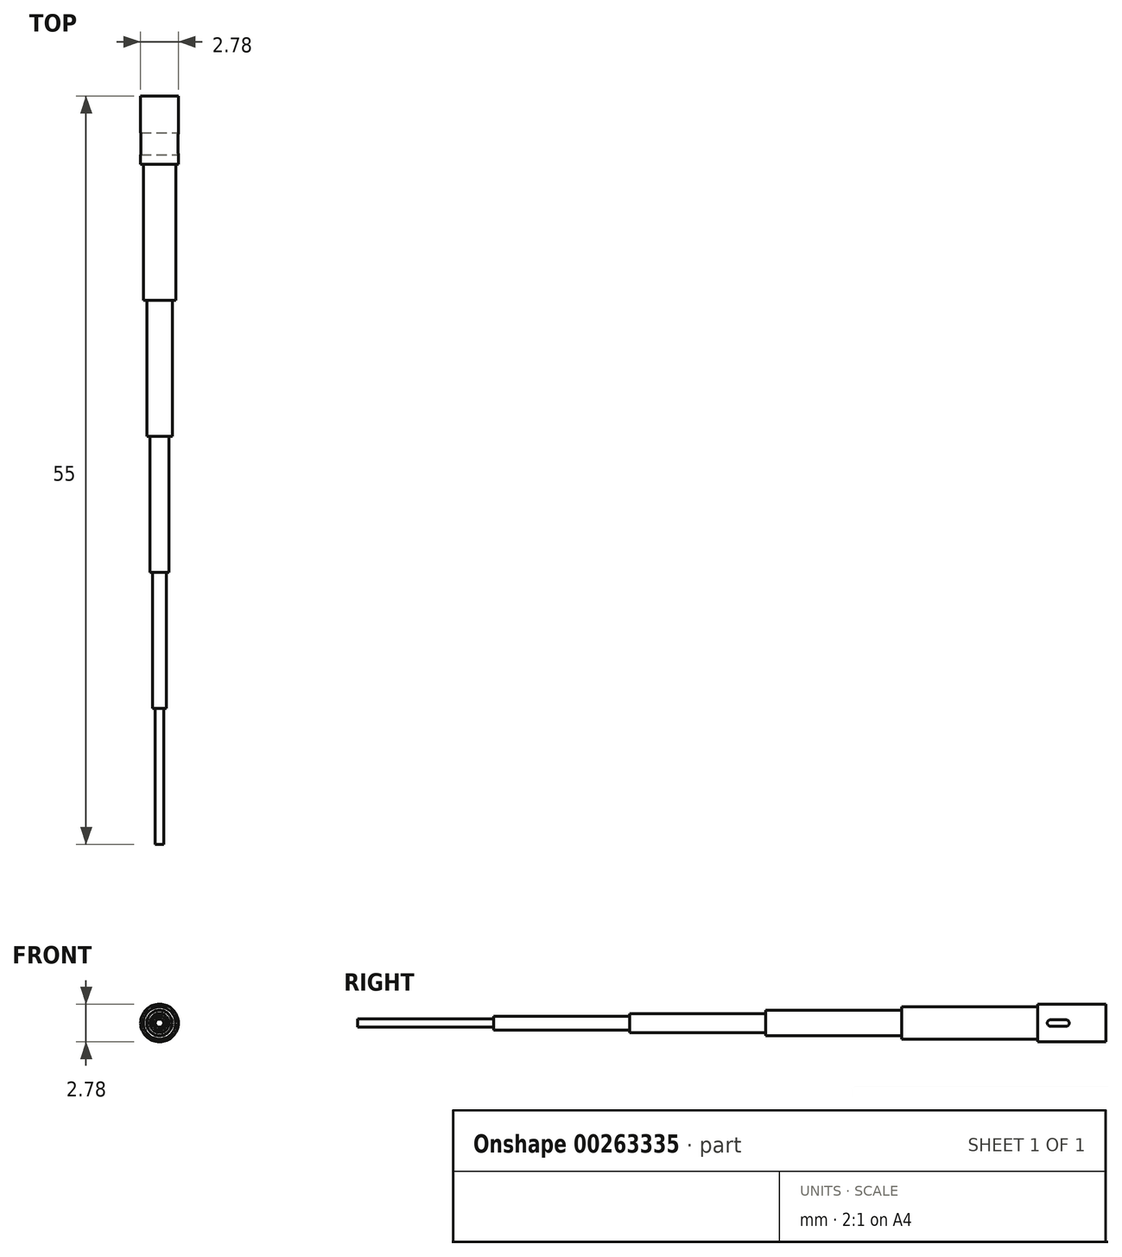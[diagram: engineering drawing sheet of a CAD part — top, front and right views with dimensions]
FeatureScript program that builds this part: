
annotation { "Feature Type Name" : "Feature", "Feature Type Description" : "" }
export const myFeature = defineFeature(function(context is Context, id is Id, definition is map)
    precondition{}
    {
        {
            var Q0;
            Q0=qCreatedBy(makeId("Front.planeOp"),FACE);
            var sketch = newSketch(context, id + "F0", { "sketchPlane" : qUnion([Q0])});
            skCircle(sketch, "E0", {"center": v(0, 0) * mm, "radius": 1.39 * mm});
            skSolve(sketch);
        }
        {
            var Q0;
            Q0=qSketchRegion(id+"F0",true);
            extrude(context, id + "F1", {"entities" : qUnion([Q0]), "depth" : 5 * mm});
        }
        {
            var Q0;
            Q0=makeQuery(id+"F1.opExtrude","CAP_FACE",FACE,{"disambiguationData":[OSD([sQuery(id+"F0.wireOp",EDGE,"E0")])],"isStart":false});
            var sketch = newSketch(context, id + "F2", { "sketchPlane" : qUnion([Q0])});
            skCircle(sketch, "E1", {"center": v(0, 0) * mm, "radius": 1.19 * mm});
            skSolve(sketch);
        }
        {
            var Q0;
            Q0=qSketchRegion(id+"F2",true);
            extrude(context, id + "F3", {"entities" : qUnion([Q0]), "operationType" : NewBodyOperationType.ADD, "depth" : 10 * mm});
        }
        {
            var Q0;
            Q0=makeQuery(id+"F3.opExtrude","CAP_FACE",FACE,{"disambiguationData":[OSD([sQuery(id+"F2.wireOp",EDGE,"E1")])],"isStart":false});
            var sketch = newSketch(context, id + "F4", { "sketchPlane" : qUnion([Q0])});
            skCircle(sketch, "E2", {"center": v(0, 0) * mm, "radius": 0.93 * mm});
            skSolve(sketch);
        }
        {
            var Q0;
            Q0=qSketchRegion(id+"F4",true);
            extrude(context, id + "F5", {"entities" : qUnion([Q0]), "operationType" : NewBodyOperationType.ADD, "depth" : 10 * mm});
        }
        {
            var Q0;
            Q0=makeQuery(id+"F5.opExtrude","CAP_FACE",FACE,{"disambiguationData":[OSD([sQuery(id+"F4.wireOp",EDGE,"E2")])],"isStart":false});
            var sketch = newSketch(context, id + "F6", { "sketchPlane" : qUnion([Q0])});
            skCircle(sketch, "E3", {"center": v(0, 0) * mm, "radius": 0.7 * mm});
            skSolve(sketch);
        }
        {
            var Q0;
            Q0=qSketchRegion(id+"F6",true);
            extrude(context, id + "F7", {"entities" : qUnion([Q0]), "operationType" : NewBodyOperationType.ADD, "depth" : 10 * mm});
        }
        {
            var Q0;
            Q0=makeQuery(id+"F7.opExtrude","CAP_FACE",FACE,{"disambiguationData":[OSD([sQuery(id+"F6.wireOp",EDGE,"E3")])],"isStart":false});
            var sketch = newSketch(context, id + "F8", { "sketchPlane" : qUnion([Q0])});
            skCircle(sketch, "E4", {"center": v(0, 0) * mm, "radius": 0.5 * mm});
            skSolve(sketch);
        }
        {
            var Q0;
            Q0=qSketchRegion(id+"F8",true);
            extrude(context, id + "F9", {"entities" : qUnion([Q0]), "operationType" : NewBodyOperationType.ADD, "depth" : 10 * mm});
        }
        {
            var Q0;
            Q0=makeQuery(id+"F9.opExtrude","CAP_FACE",FACE,{"disambiguationData":[OSD([sQuery(id+"F8.wireOp",EDGE,"E4")])],"isStart":false});
            var sketch = newSketch(context, id + "F10", { "sketchPlane" : qUnion([Q0])});
            skCircle(sketch, "E5", {"center": v(0, 0) * mm, "radius": 0.3 * mm});
            skSolve(sketch);
        }
        {
            var Q0;
            Q0=qSketchRegion(id+"F10",true);
            extrude(context, id + "F11", {"entities" : qUnion([Q0]), "operationType" : NewBodyOperationType.ADD, "depth" : 10 * mm});
        }
        {
            var Q0;
            Q0=qCreatedBy(makeId("Right.planeOp"),FACE);
            var sketch = newSketch(context, id + "F12", { "sketchPlane" : qUnion([Q0])});
            skArc(sketch, "E6", {"start": v(-4.07, 0.23) * mm, "mid": v(-4.3, 0) * mm, "end": v(-4.07, -0.23) * mm});
            skPoint(sketch, "E7.center.orphan", {"position": v(-3.84, 0) * mm});
            skArc(sketch, "E8", {"start": v(-2.9, -0.23) * mm, "mid": v(-2.68, 0) * mm, "end": v(-2.9, 0.23) * mm});
            skPoint(sketch, "E9.center.orphan", {"position": v(-3.6, 0) * mm});
            skPoint(sketch, "E10.center.orphan", {"position": v(-3.14, 0) * mm});
            skPoint(sketch, "E11.center.orphan", {"position": v(-3.37, 0) * mm});
            skLineSegment(sketch, "E12", {"start": v(-2.9, 0.23) * mm, "end": v(-4.07, 0.23) * mm});
            skLineSegment(sketch, "E13", {"start": v(-2.9, -0.23) * mm, "end": v(-4.07, -0.23) * mm});
            skSolve(sketch);
        }
        {
            var Q0;
            Q0=qSketchRegion(id+"F12",true);
            extrude(context, id + "F13", {"entities" : qUnion([Q0]), "operationType" : NewBodyOperationType.REMOVE, "endBound" : BoundingType.SYMMETRIC, "oppositeDirection" : true, "depth" : 25 * mm});
        }
    });
